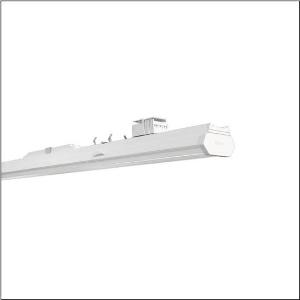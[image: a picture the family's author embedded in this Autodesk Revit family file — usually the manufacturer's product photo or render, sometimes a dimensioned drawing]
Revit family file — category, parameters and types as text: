
# Revit family: licross_11_protected_mo_51tp11dn695g
name_source: partatom
category: Lighting Fixtures
units: mm (PartAtom-declared; Revit-internal decimal feet)

## family parameters
Cut with Voids When Loaded = No
Host = Face
Light Source = No
Part Type = Normal
Room Calculation Point = No
Round Connector Dimension = Use Diameter
Shared = No

## types (1)
- --- (1 x LED, 9680 lm, 57.1 W, 6500K)
    Apparent Load = 57 VA
    CIE Flux Codes = 83 94 98 100 100
    Color Rendering = 80
    Color Temperature = 6500K
    Default Elevation = 1800 mm
    Description = Licross 11 Protected MO, luminaire insert, of sheet steel, galvanised, coil coated, white, length: 1.500mm, width: 90mm, height: 101mm, LED rated luminous flux: 9.680lm, light colour: 865, SDCM (Standard Deviation of Colour Matching)MacAdam ≤ 2 SDCM (initial), control gear: DALI 2, with plug, 5-pole, with phase selection, mains connection: 220..240V, AC, 50/60Hz, rated input power: 57W, internal wiring halogen-free, primary light control with lens, of plastic, primary optical cover: cover, of PMMA, light emission: direct distribution, primary light characteristic: symmetric, protection rating (complete): IP64, insulation class (complete): insulation class I (protective earthing), certification: CE, ENEC, VDE, UKCA, protection symbol: D if used in an environment with conductive dust loads with corresponding accessories, impact resistance: IK06, permissible ambient temperature for indoor applications: -25..+35°C, corresponds to IFS (International Featured Standards) requirements for safety and quality in the food industry, reducing of maximum allowable ambient temperature of 5°C with ceiling mounting, LABS conformity tested according to VDMA 24364:2018-05, The light source and the operating device comply with the requirements of the Ecodesign Regulation (EU) 2019/2020 and are replaceable in accordance with this regulation, packaging unit: 1 piece
    Height = 92 mm
    Lamp = 1 x LED
    Lamp Light Flux = 9680 lm
    Lamp Power = 57.1 W
    Lamp count = 1
    Length = 1500 mm
    Luminous efficacy = 170 lm/W
    Manufacturer = Siteco
    ModVariant = No
    Model = 51TP11DN695G
    Mounting Place = Ceiling
    Mounting Type = Pendant
    Number of Poles = 1
    OnlyDefault = Yes
    Power Factor = 1
    Product Name = Licross 11 Protected MO
    Product group = luminaire insert | ceiling pendant
    ProductGroupID = 901
    Protection Class = Protection class I
    Protection Degree = IP 64
    RLX_Detail_Level = 1
    RLX_Emergency_Light_Flux = 0 lm
    RLX_Emergency_Type = 0
    RLX_Emergency_Type_DB = No
    RlxData = <blob elided: 24441 chars, md5=9b6fce5e>
    Socket = socket
    Standby Power = 0 W
    System Light Flux = 9680 lm
    System Power = 57 W
    Type Comments = factory setting: luminous flux: 100 % | dim-lin: 254 | 378 mA
    Type Image = l_1256148.jpg
    URL = http://relux.com
    VarID = @adj_057677
    Voltage = 0 V
    Weight = 0.00 kg
    Width = 88 mm

## geometry (parser evidence)
native form markers: Blend x4, Sweep x11
no freeform markers — native parametric forms only
